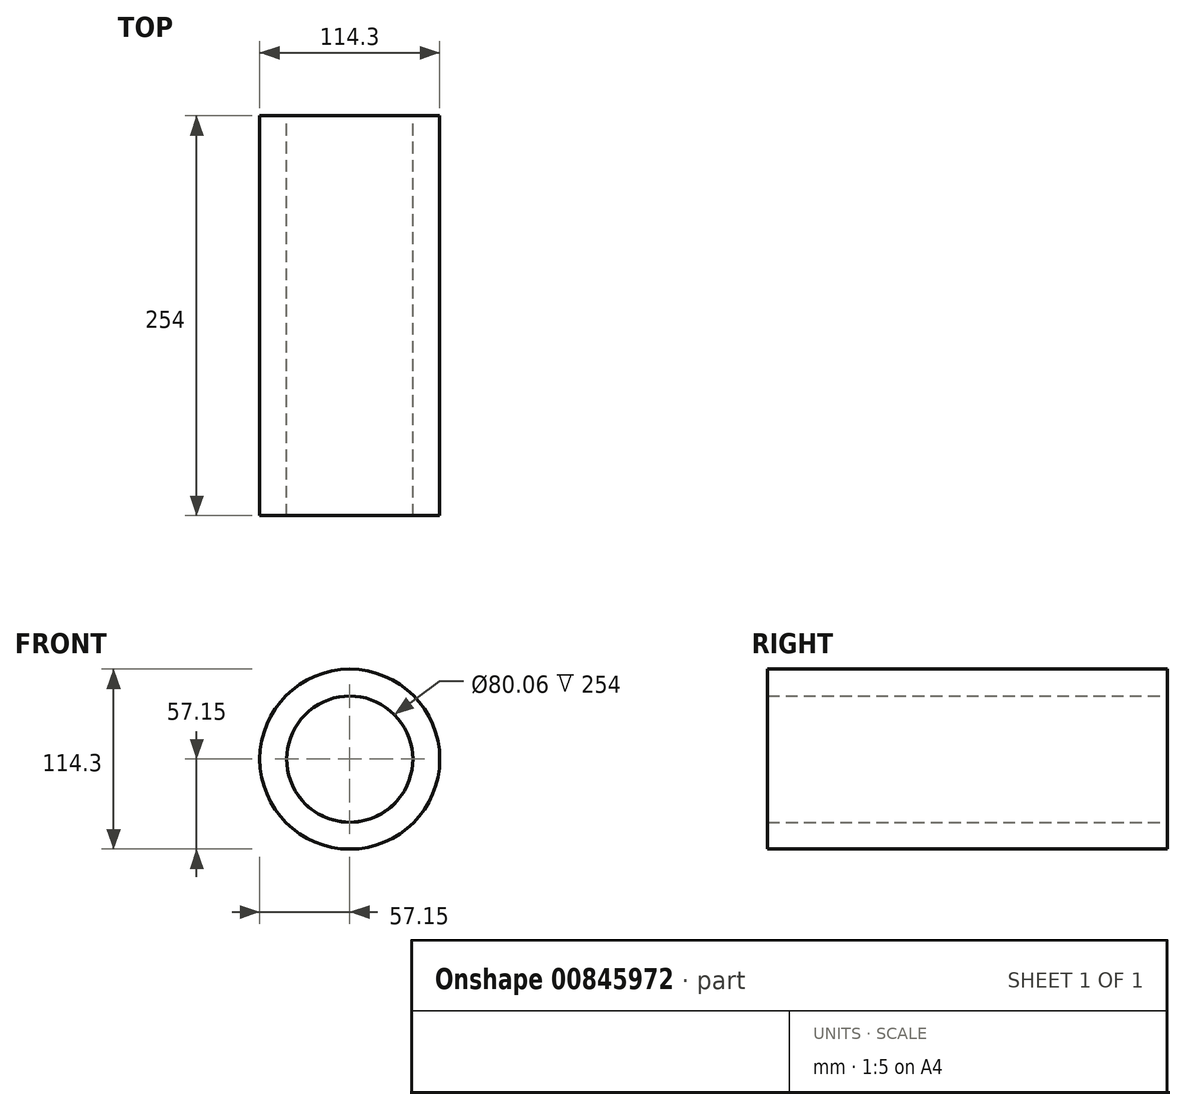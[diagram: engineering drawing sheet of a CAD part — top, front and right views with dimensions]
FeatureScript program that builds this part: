
annotation { "Feature Type Name" : "Feature", "Feature Type Description" : "" }
export const myFeature = defineFeature(function(context is Context, id is Id, definition is map)
    precondition{}
    {
        {
            var Q0;
            Q0=qCreatedBy(makeId("Front.planeOp"),FACE);
            var sketch = newSketch(context, id + "F0", { "sketchPlane" : qUnion([Q0])});
            skCircle(sketch, "E0", {"center": v(0, 0) * mm, "radius": 57.15 * mm});
            skCircle(sketch, "E1", {"center": v(0, 0) * mm, "radius": 40.03 * mm});
            skSolve(sketch);
        }
        {
            var Q0;
            Q0=makeQuery(id+"F0.imprint","IMPRINT",FACE,{"disambiguationData":[TD([[makeQuery(id+"F0.imprint","IMPRINT",EDGE,{"derivedFrom":sQuery(id+"F0.wireOp",EDGE,"E0")}),1.0]])]});
            extrude(context, id + "F1", {"entities" : qUnion([Q0]), "depth" : 254 * mm, "offsetDistance" : 25.4 * mm});
        }
        {
            var Q0;
            Q0=makeQuery(id+"F1.opExtrude","CAP_FACE",FACE,{"disambiguationData":[OSD([sQuery(id+"F0.wireOp",EDGE,"E0"),sQuery(id+"F0.wireOp",EDGE,"E1")])],"isStart":false});
            var sketch = newSketch(context, id + "F2", { "sketchPlane" : qUnion([Q0])});
            skPoint(sketch, "E2", {"position": v(-34.67, -20.02) * mm});
            skPoint(sketch, "E3", {"position": v(34.67, -20.02) * mm});
            skLineSegment(sketch, "E4", {"start": v(-34.67, -20.02) * mm, "end": v(0, 0) * mm, "construction": true});
            skLineSegment(sketch, "E5", {"start": v(34.67, -20.02) * mm, "end": v(0, 0) * mm, "construction": true});
            skArc(sketch, "E6.0", {"start": v(-34.67, -20.02) * mm, "mid": v(0, -40.03) * mm, "end": v(34.67, -20.02) * mm});
            skArc(sketch, "E7", {"start": v(-34.72, -20.05) * mm, "mid": v(0, -40.1) * mm, "end": v(34.72, -20.05) * mm});
            skLineSegment(sketch, "E8", {"start": v(-34.67, -20.02) * mm, "end": v(-34.72, -20.05) * mm});
            skLineSegment(sketch, "E9", {"start": v(34.67, -20.02) * mm, "end": v(34.72, -20.05) * mm});
            skSolve(sketch);
        }
        {
            var Q0;
            Q0=makeQuery(id+"F2.imprint","IMPRINT",FACE,{"disambiguationData":[TD([[makeQuery(id+"F2.imprint","IMPRINT",EDGE,{"derivedFrom":sQuery(id+"F2.wireOp",EDGE,"E6.0")}),-1.0]])]});
            extrude(context, id + "F3", {"entities" : qUnion([Q0]), "operationType" : NewBodyOperationType.REMOVE, "oppositeDirection" : true, "depth" : 0.13 * mm, "offsetDistance" : 25.4 * mm});
        }
    });
